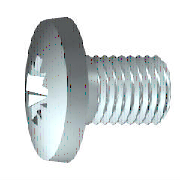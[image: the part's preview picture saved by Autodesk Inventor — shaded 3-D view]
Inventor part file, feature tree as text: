
AUTODESK INVENTOR PART (.ipt)
format: ipt  version: 2015 (Build 190159000, 159)  size: 219,136 bytes
history: native  units: mm (DEFAULTED — no unit token found)
features: other x3, chamfer x2, fillet x2, sketch x2, revolve x1, extrude x1, pattern_circular x1
ambient origin geometry x8: Origin, YZ Plane, XZ Plane, XY Plane, X Axis, Y Axis, Z Axis, Center Point
bodies: Solid1 (feature_tree)
feature tree (12):
  revolve  "Revolution1"  [1 undecoded]
  chamfer  "Chamfer1"  Distance=0.15mm
  chamfer  "Chamfer2"  Distance=0.15mm
  fillet  "Fillet1"  Radius=0.3mm
  extrude  "Extrusion1"  Depth=0.666667mm
  pattern_circular  "PolarArray1"  [2 undecoded]
  fillet  "Fillet2"  Radius=2.08mm
  other  "MSC_A1"
  other  "MSC_PF1"
  other  "MSC_PT1"
  sketch  "Sketch2"  dims[d6=3.2mm d9=0.872665mm]
  sketch  "Sketch3"  dims[d10=90.0deg d11=0.15mm d12=0.15mm d13=0.3mm d14=0.3mm d16=10.0mm d17=0.0mm d19=2.08mm d20=0.8mm d21=2.82mm d22=0.8mm d23=0.0mm d24=40.0mm d26=360.0deg d27=0.0mm d28=0.0mm d29=0.0mm d34=0.666667mm d35=45.0deg d36=45.0deg d38=0.0mm d39=0.0mm]
note: 3 required parameter values undecoded (feature->parameter linkage not recoverable at this tier; creation-order binding heuristic only, values carry confidence <= 0.55)